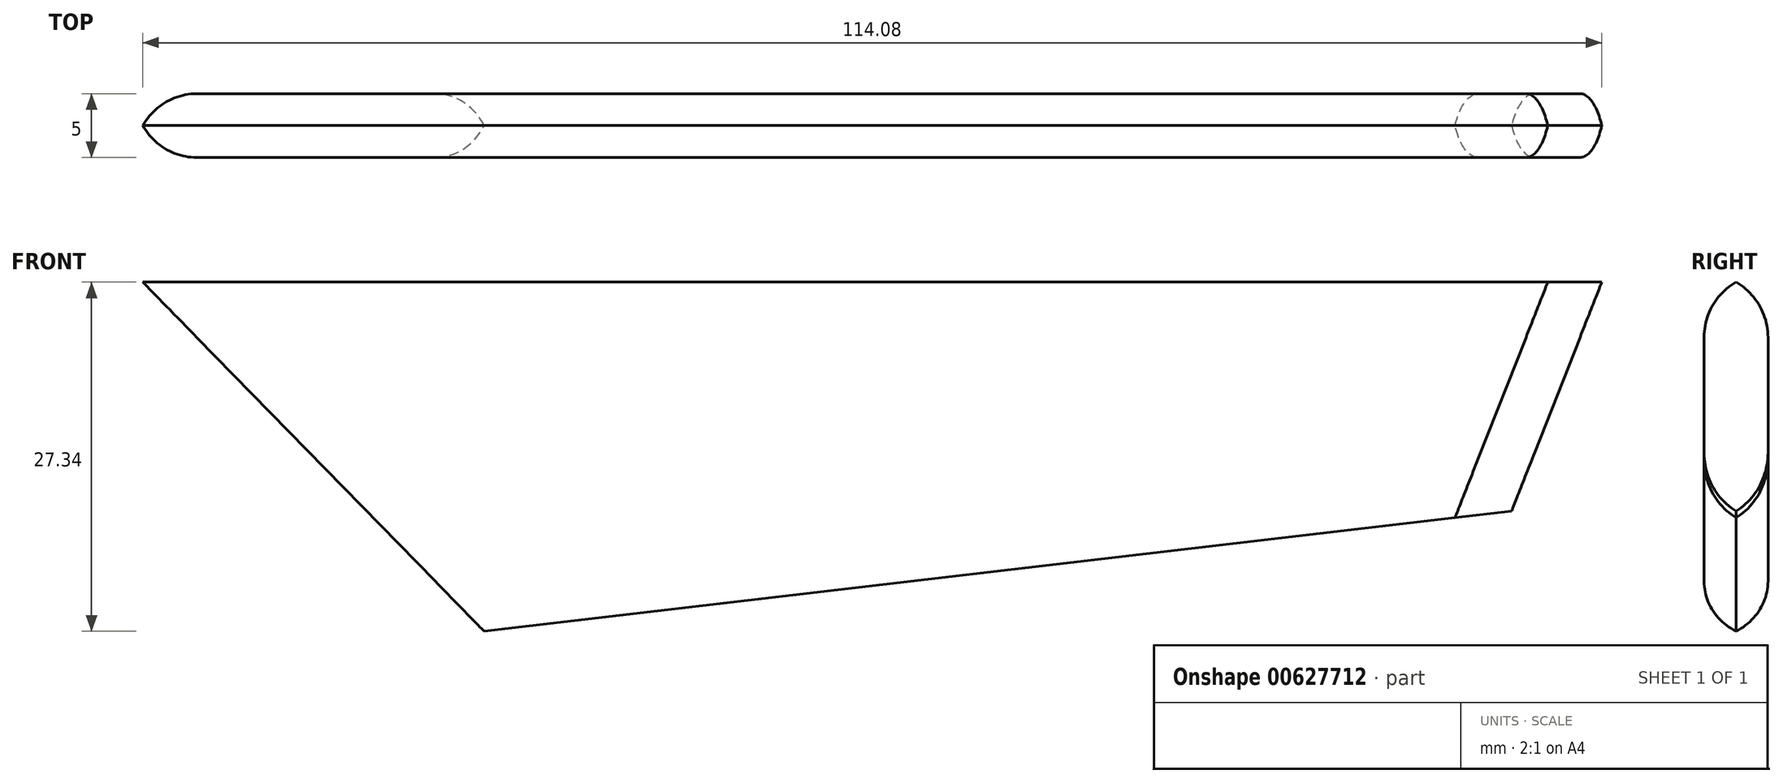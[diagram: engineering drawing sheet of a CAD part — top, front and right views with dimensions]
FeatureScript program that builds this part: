
annotation { "Feature Type Name" : "Feature", "Feature Type Description" : "" }
export const myFeature = defineFeature(function(context is Context, id is Id, definition is map)
    precondition{}
    {
        {
            var Q0;
            Q0=qCreatedBy(makeId("Front.planeOp"),FACE);
            var sketch = newSketch(context, id + "F0", { "sketchPlane" : qUnion([Q0])});
            skLineSegment(sketch, "E0", {"start": v(-47.56, 0) * mm, "end": v(-19.62, -28.62) * mm});
            skLineSegment(sketch, "E1", {"start": v(-19.62, -28.62) * mm, "end": v(59.84, -19.3) * mm});
            skLineSegment(sketch, "E2", {"start": v(59.84, -19.3) * mm, "end": v(67.44, 0) * mm});
            skLineSegment(sketch, "E3", {"start": v(-47.56, 0) * mm, "end": v(67.44, 0) * mm});
            skFitSpline(sketch, "E4", {"points": [v(67.44, 0) * mm, v(70.88, -4.57) * mm], "startDerivative": vector(11.5, 0) * mm, "endDerivative": vector(-1.2, -3.03) * mm});
            skFitSpline(sketch, "E5", {"points": [v(59.84, -19.3) * mm, v(70.9, -4.5) * mm], "startDerivative": vector(8.2, 3.7) * mm, "endDerivative": vector(4.86, 12.37) * mm});
            skLineSegment(sketch, "E6", {"start": v(63.22, 0) * mm, "end": v(55.42, -19.82) * mm});
            skSolve(sketch);
        }
        {
            var Q0;
            Q0=makeQuery(id+"F0.imprint","IMPRINT",FACE,{"disambiguationData":[TD([[makeQuery(id+"F0.imprint","IMPRINT",EDGE,{"derivedFrom":sQuery(id+"F0.wireOp",EDGE,"E0")}),1.0]])]});
            extrude(context, id + "F1", {"entities" : qUnion([Q0]), "endBound" : BoundingType.SYMMETRIC, "depth" : 5 * mm, "offsetDistance" : 25 * mm});
        }
        {
            var Q0;
            Q0=makeQuery(id+"F1.opExtrude","CAP_EDGE",EDGE,{"disambiguationData":[OSD([sQuery(id+"F0.wireOp",EDGE,"E3")])],"isStart":false});
            var Q1;
            Q1=makeQuery(id+"F1.opExtrude","CAP_EDGE",EDGE,{"disambiguationData":[OSD([sQuery(id+"F0.wireOp",EDGE,"E1")])],"isStart":false});
            var Q2;
            Q2=makeQuery(id+"F1.opExtrude","CAP_EDGE",EDGE,{"disambiguationData":[OSD([sQuery(id+"F0.wireOp",EDGE,"E1")])],"isStart":true});
            var Q3;
            Q3=makeQuery(id+"F1.opExtrude","CAP_EDGE",EDGE,{"disambiguationData":[OSD([sQuery(id+"F0.wireOp",EDGE,"E3")])],"isStart":true});
            fillet(context, id + "F2", {"entities" : qUnion([Q0, Q1, Q2, Q3]), "radius" : 5 * mm, "tangentPropagation" : true, "allowEdgeOverflow" : false});
        }
        {
            var Q0;
            {var subQ0=sQuery(id+"F0.wireOp",EDGE,"E2");Q0=makeQuery(id+"F0.imprint","IMPRINT",FACE,{"disambiguationData":[TD([[makeQuery(id+"F0.imprint","IMPRINT",EDGE,{"derivedFrom":subQ0}),1.0]])]});}
            extrude(context, id + "F3", {"entities" : qUnion([Q0]), "endBound" : BoundingType.SYMMETRIC, "depth" : 5 * mm, "offsetDistance" : 25 * mm});
        }
        {
            var Q0;
            Q0=makeQuery(id+"F3.opExtrude","CAP_EDGE",EDGE,{"disambiguationData":[OSD([sQuery(id+"F0.wireOp",EDGE,"E3")])],"isStart":false});
            var Q1;
            Q1=makeQuery(id+"F3.opExtrude","CAP_EDGE",EDGE,{"disambiguationData":[OSD([sQuery(id+"F0.wireOp",EDGE,"E1")])],"isStart":false});
            var Q2;
            Q2=makeQuery(id+"F3.opExtrude","CAP_EDGE",EDGE,{"disambiguationData":[OSD([sQuery(id+"F0.wireOp",EDGE,"E1")])],"isStart":true});
            var Q3;
            Q3=makeQuery(id+"F3.opExtrude","CAP_EDGE",EDGE,{"disambiguationData":[OSD([sQuery(id+"F0.wireOp",EDGE,"E3")])],"isStart":true});
            fillet(context, id + "F4", {"entities" : qUnion([Q0, Q1, Q2, Q3]), "radius" : 5 * mm, "tangentPropagation" : true, "allowEdgeOverflow" : false});
        }
    });
